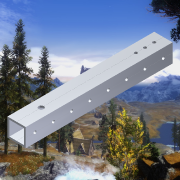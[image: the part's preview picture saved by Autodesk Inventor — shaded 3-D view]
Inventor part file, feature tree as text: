
AUTODESK INVENTOR PART (.ipt)
format: ipt  version: 2,015 SP1 (Build 190203100, 203)  size: 1,199,104 bytes
history: native  units: in
note: dims shown in document units (in); Inventor stores cm internally (conversion verified against a paired STEP export)
features: sketch x4, plane x2, extrude x2, hole x2, pattern_circular x1, other x1, imported_body x1, projected_geometry x1, reference x1
ambient origin geometry x8: Origin, YZ Plane, XZ Plane, XY Plane, X Axis, Y Axis, Z Axis, Center Point
bodies: Body1 (feature_tree)
feature tree (15):
  pattern_circular  "CirPattern2"
  other  "VersaFrame 1 x 1 x 0.100 Pre-Drilled Tube Stock (59 length)(217-4104)1"
  plane  "Work Plane1"
  extrude  "Extrusion1"  Depth=3936.9685in TaperAngle=0.0deg
  extrude  "Extrusion2"  Depth=1.0in
  plane  "Work Plane2"
  hole  "Hole2"  [1 undecoded]
  hole  "Hole3"  [1 undecoded]
  imported_body  "Base1"
  sketch  "Sketch1"  dims[d0=9.0in d1=3936.9685in d2=0.0in]
  sketch  "Sketch3"  dims[d10=1.0in d11=0.0in]
  projected_geometry  "Projected Loop4"
  sketch  "Sketch4"  dims[d13=0.281in d14=0.75in d15=0.375in d16=0.25in d17=0.5635in d18=1.0in d19=0.8108in d20=0.5in]
  sketch  "Sketch5"  dims[d23=1.0in d27=0.163in d28=0.75in d29=0.375in d30=0.25in d31=0.5635in d32=1.0in d33=0.8108in d34=0.5in]
  reference  "Reference3"
note: 2 required parameter values undecoded (feature->parameter linkage not recoverable at this tier; creation-order binding heuristic only, values carry confidence <= 0.55)
